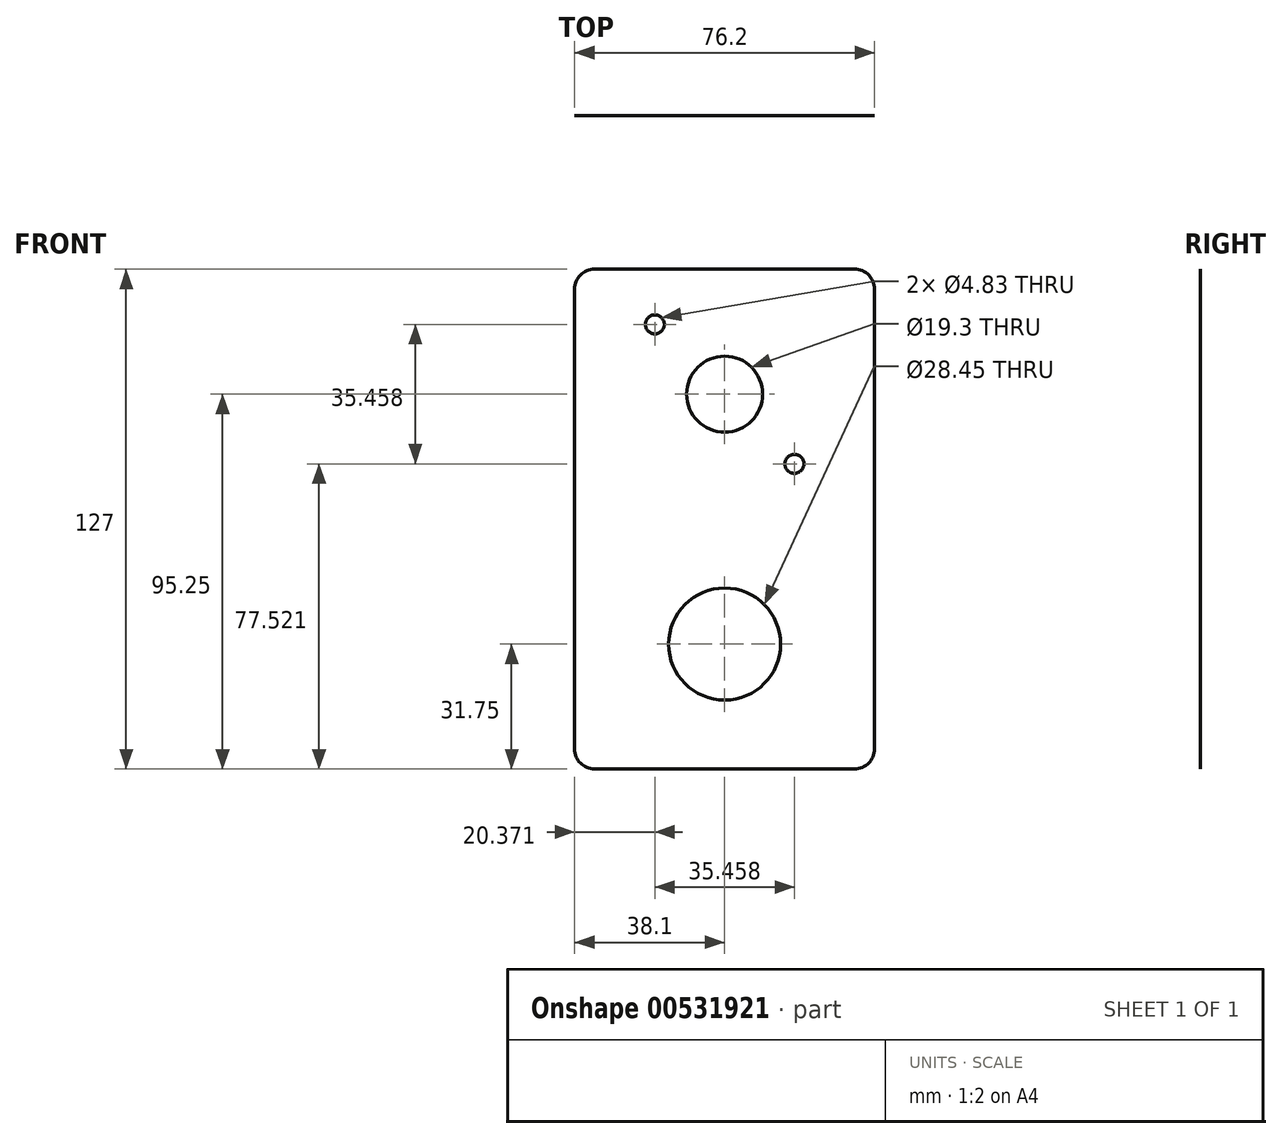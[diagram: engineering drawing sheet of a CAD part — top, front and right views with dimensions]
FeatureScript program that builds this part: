
annotation { "Feature Type Name" : "Feature", "Feature Type Description" : "" }
export const myFeature = defineFeature(function(context is Context, id is Id, definition is map)
    precondition{}
    {
        {
            var Q0;
            Q0=qCreatedBy(makeId("Front.planeOp"),FACE);
            var sketch = newSketch(context, id + "F0", { "sketchPlane" : qUnion([Q0])});
            skCircle(sketch, "E0", {"center": v(0, 0) * mm, "radius": 9.65 * mm});
            skLineSegment(sketch, "E1.bottom", {"start": v(17.73, -17.73) * mm, "end": v(-17.73, -17.73) * mm, "construction": true});
            skLineSegment(sketch, "E1.top", {"start": v(17.73, 17.73) * mm, "end": v(-17.73, 17.73) * mm, "construction": true});
            skLineSegment(sketch, "E1.left", {"start": v(17.73, -17.73) * mm, "end": v(17.73, 17.73) * mm, "construction": true});
            skLineSegment(sketch, "E1.right", {"start": v(-17.73, -17.73) * mm, "end": v(-17.73, 17.73) * mm, "construction": true});
            skCircle(sketch, "E2", {"center": v(-17.73, 17.73) * mm, "radius": 2.41 * mm});
            skCircle(sketch, "E3", {"center": v(17.73, -17.73) * mm, "radius": 2.41 * mm});
            skLineSegment(sketch, "E4", {"start": v(0, 0) * mm, "end": v(0, -63.5) * mm, "construction": true});
            skCircle(sketch, "E5", {"center": v(0, -63.5) * mm, "radius": 14.22 * mm});
            skPoint(sketch, "E6", {"position": v(0, -31.75) * mm});
            skLineSegment(sketch, "E7.bottom", {"start": v(38.1, -95.25) * mm, "end": v(-38.1, -95.25) * mm});
            skLineSegment(sketch, "E7.top", {"start": v(38.1, 31.75) * mm, "end": v(-38.1, 31.75) * mm});
            skLineSegment(sketch, "E7.left", {"start": v(38.1, -95.25) * mm, "end": v(38.1, 31.75) * mm});
            skCircle(sketch, "E8", {"center": v(0, -63.5) * mm, "radius": 31.75 * mm, "construction": true});
            skCircle(sketch, "E9", {"center": v(0, 0) * mm, "radius": 31.75 * mm, "construction": true});
            skLineSegment(sketch, "E10", {"start": v(-38.1, 31.75) * mm, "end": v(-38.1, -95.25) * mm});
            skLineSegment(sketch, "E11.bottom", {"start": v(38.1, -77.76) * mm, "end": v(44.45, -77.76) * mm});
            skLineSegment(sketch, "E11.top", {"start": v(38.1, -65.06) * mm, "end": v(44.45, -65.06) * mm});
            skLineSegment(sketch, "E11.left", {"start": v(38.1, -77.76) * mm, "end": v(38.1, -65.06) * mm});
            skLineSegment(sketch, "E11.right", {"start": v(44.45, -77.76) * mm, "end": v(44.45, -65.06) * mm});
            skSolve(sketch);
        }
        {
            var Q0;
            Q0=makeQuery(id+"F0.imprint","IMPRINT",FACE,{"disambiguationData":[TD([[makeQuery(id+"F0.imprint","IMPRINT",EDGE,{"derivedFrom":sQuery(id+"F0.wireOp",EDGE,"E0")}),-1.0]])]});
            extrude(context, id + "F1", {"entities" : qUnion([Q0]), "depth" : 1 / 203.2 * mm, "offsetDistance" : 25.4 * mm});
        }
        {
            var Q0;
            Q0=makeQuery(id+"F1.opExtrude","SWEPT_EDGE",EDGE,{"disambiguationData":[OSD([sQuery(id+"F0.wireOp",EDGE,"E7.bottom"),sQuery(id+"F0.wireOp",EDGE,"E7.right")])]});
            var Q1;
            Q1=makeQuery(id+"F1.opExtrude","SWEPT_EDGE",EDGE,{"disambiguationData":[OSD([sQuery(id+"F0.wireOp",EDGE,"E7.bottom"),sQuery(id+"F0.wireOp",EDGE,"E7.left")])]});
            var Q2;
            Q2=makeQuery(id+"F1.opExtrude","SWEPT_EDGE",EDGE,{"disambiguationData":[OSD([sQuery(id+"F0.wireOp",EDGE,"E7.top"),sQuery(id+"F0.wireOp",EDGE,"E7.left")])]});
            var Q3;
            Q3=makeQuery(id+"F1.opExtrude","SWEPT_EDGE",EDGE,{"disambiguationData":[OSD([sQuery(id+"F0.wireOp",EDGE,"E7.top"),sQuery(id+"F0.wireOp",EDGE,"E7.right")])]});
            fillet(context, id + "F2", {"entities" : qUnion([Q0, Q1, Q2, Q3]), "radius" : 5.08 * mm, "tangentPropagation" : true, "allowEdgeOverflow" : false});
        }
    });
